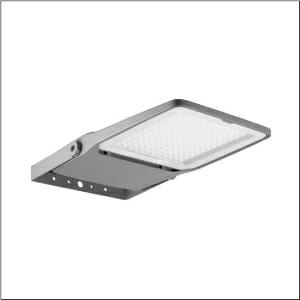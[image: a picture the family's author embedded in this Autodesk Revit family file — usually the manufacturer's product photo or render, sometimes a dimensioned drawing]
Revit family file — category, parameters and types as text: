
# Revit family: floodlight_fl_20_midi___pl52_5xa7682e1d2ac_40bd
name_source: partatom
category: Lighting Fixtures
units: mm (PartAtom-declared; Revit-internal decimal feet)

## family parameters
Cut with Voids When Loaded = No
Host = Face
Light Source = No
Part Type = Normal
Room Calculation Point = No
Round Connector Dimension = Use Diameter
Shared = No

## types (1)
- --- (1 x LED 3000K / CRI = 80 (unbekannt), 21030 lm, 3000K)
    Apparent Load = 208 VA
    CIE Flux Codes = 27 59 98 100 100
    Color Rendering = 80
    Color Temperature = 3000K
    Default Elevation = 1800 mm
    Description = Floodlight FL 20 midi, floodlight, primary light control with lens, of plastic, primary optical cover: protective disc, of toughened safety glass, transparent, light distribution: PL52, light emission: direct distribution, primary light characteristic: asymmetric, installation type: surface-mounted, LED, High Power LED, rated luminous flux: 21.030lm, luminous efficacy: 101lm/W, light colour: 830, colour temperature: 3000K, control gear: ECG Plus, control: flexible luminous flux parameterisation, time-dependent luminous flux control, digital communication interface, power reduction, overheat protection, electronic power reduction, with terminal, 5-pole, max. 2.5mm², mains connection: 220..240V, AC, 50/60Hz, rated input power: 208W, LED unit, of diecast aluminium, powder-coated, Siteco® metallic grey (DB 702S), corrosivity category C5 mid according to DIN EN ISO 12944, incl. 1x M20 cable gland for cable Ø 6.5..12mm, length: 731mm, width: 450mm, height: 76mm, housing frame, of diecast aluminium, powder-coated, Siteco® metallic grey (DB 702S), wall fastening, of steel, powder-coated, Siteco® metallic grey (DB 702S), DALI, protection rating (complete): IP66, insulation class (complete): insulation class II (safety insulation), certification: CE, ENEC, VDE, protection symbol: D, permissible operating ambient temperature: -40..+40°C, permissible operating ambient temperature for outdoor applications: -40..+50°C, standard: DIN EN 12944, packaging unit: 1 piece

Light Distribution: PL52
    Height = 76 mm
    Lamp = 1 x LED 3000K / CRI >= 80 (unbekannt)
    Lamp Light Flux = 21030 lm
    Lamp count = 1
    Length = 731 mm
    Luminous efficacy = 101 lm/W
    Manufacturer = Siteco
    ModVariant = No
    Model = 5XA7682E1D2AC
    Mounting Place = Wall
    Mounting Type = Surface mounted
    Number of Poles = 1
    OnlyDefault = Yes
    Power Factor = 1
    Product Name = Floodlight FL 20 midi | PL52
    Product group = floodlight | wall mounted
    ProductGroupID = 2001
    Protection Class = Protection class II
    Protection Degree = IP 66
    RLX_Detail_Level = 1
    RLX_Emergency_Light_Flux = 0 lm
    RLX_Emergency_Type = 0
    RLX_Emergency_Type_DB = No
    RlxData = <blob elided: 92485 chars, md5=117868ed>
    Socket = socket
    Standby Power = 0 W
    System Light Flux = 21030 lm
    System Power = 208 W
    Type Comments = factory setting: luminous flux: 100 % | dim-lin: 254 | 484 mA
    Type Image = l_1005944.jpg
    URL = http://relux.com
    VarID = @adj_147679
    Voltage = 0 V
    Weight = 0.00 kg
    Width = 450 mm

## geometry (parser evidence)
native form markers: Blend x4, Sweep x13
no freeform markers — native parametric forms only
